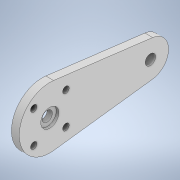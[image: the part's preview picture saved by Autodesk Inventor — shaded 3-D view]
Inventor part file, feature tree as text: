
AUTODESK INVENTOR PART (.ipt)
format: ipt  version: 2020 (Build 240168000, 168)  size: 158,208 bytes
history: native  units: mm
features: extrude x3, sketch x3, projected_geometry x1
ambient origin geometry x8: Origin, YZ Plane, XZ Plane, XY Plane, X Axis, Y Axis, Z Axis, Center Point
bodies: Body1 (feature_tree)
feature tree (7):
  extrude  "Выдавливание4"  Depth=18.6mm
  extrude  "Выдавливание5"  Depth=12.2mm
  extrude  "Выдавливание6"  Depth=9.7mm
  sketch  "Эскиз1"
  sketch  "Эскиз4"
  projected_geometry  "Спроецированная петля3"
  sketch  "Эскиз5"
